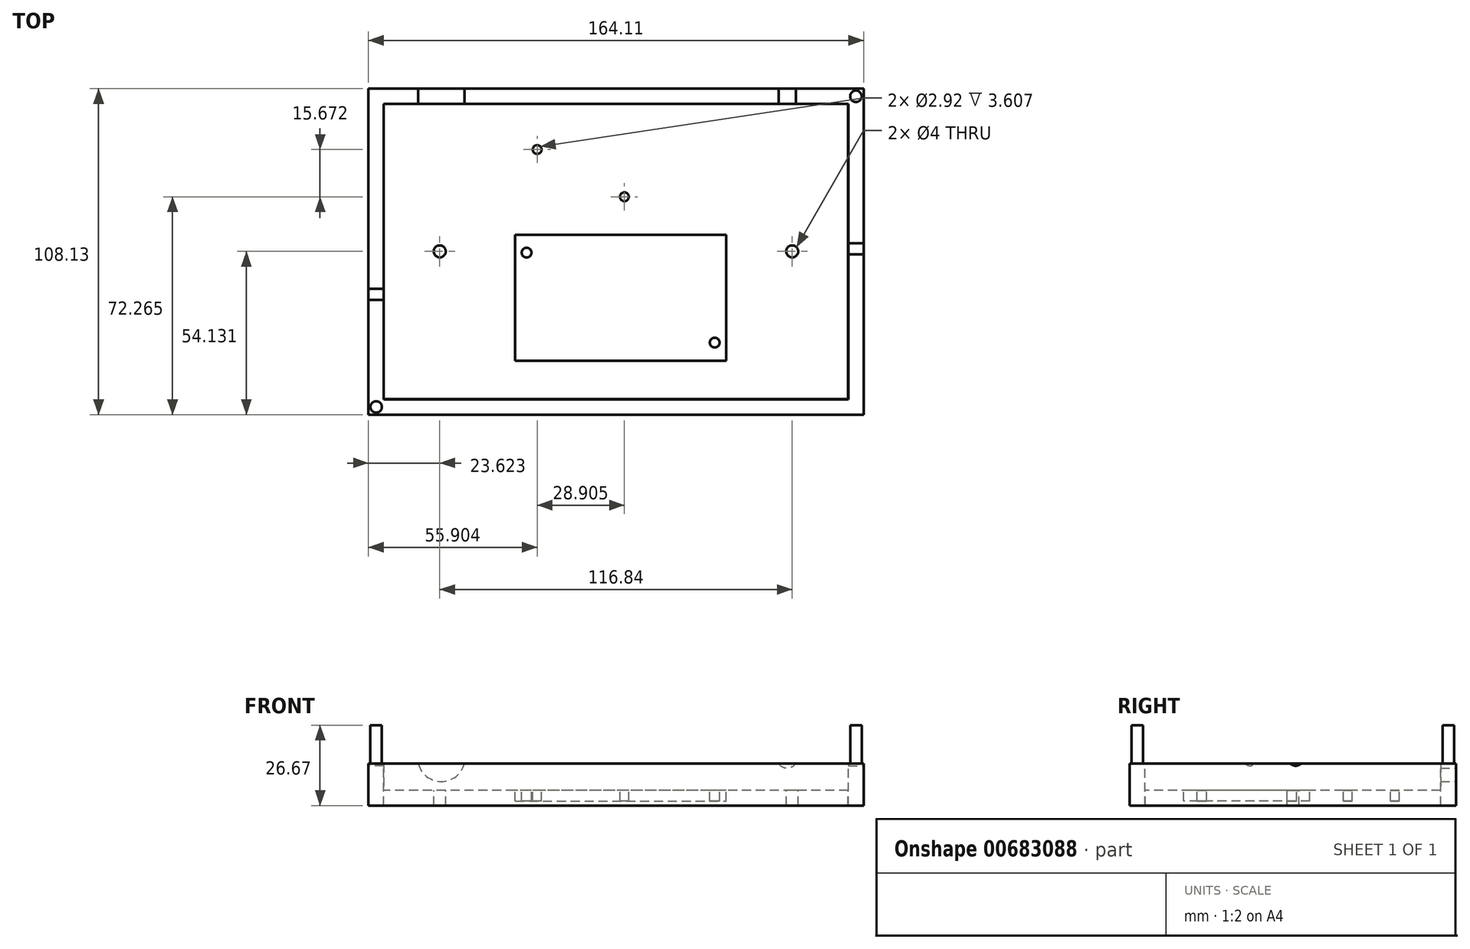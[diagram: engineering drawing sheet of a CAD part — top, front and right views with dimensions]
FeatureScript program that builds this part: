
annotation { "Feature Type Name" : "Feature", "Feature Type Description" : "" }
export const myFeature = defineFeature(function(context is Context, id is Id, definition is map)
    precondition{}
    {
        {
            var Q0;
            Q0=qCreatedBy(makeId("Top.planeOp"),FACE);
            var sketch = newSketch(context, id + "F0", { "sketchPlane" : qUnion([Q0])});
            skLineSegment(sketch, "E0", {"start": v(0, 0) * mm, "end": v(69.88, 0) * mm});
            skLineSegment(sketch, "E1", {"start": v(69.88, 0) * mm, "end": v(69.88, 41.78) * mm});
            skLineSegment(sketch, "E2", {"start": v(69.88, 41.78) * mm, "end": v(0, 41.78) * mm});
            skLineSegment(sketch, "E3", {"start": v(0, 41.78) * mm, "end": v(0, 0) * mm});
            skPoint(sketch, "E4", {"position": v(34.94, 20.9) * mm});
            skCircle(sketch, "E5", {"center": v(66.12, 35.81) * mm, "radius": 1.61 * mm});
            skCircle(sketch, "E6.MirrorC", {"center": v(3.76, 35.81) * mm, "radius": 1.61 * mm});
            skCircle(sketch, "E7.MirrorC", {"center": v(66.12, 5.97) * mm, "radius": 1.61 * mm});
            skCircle(sketch, "E8.MirrorC", {"center": v(3.76, 5.97) * mm, "radius": 1.61 * mm});
            skSolve(sketch);
        }
        {
            var Q0;
            Q0=qCreatedBy(makeId("Top.planeOp"),FACE);
            var sketch = newSketch(context, id + "F1", { "sketchPlane" : qUnion([Q0])});
            skLineSegment(sketch, "E9", {"start": v(0, 51.81) * mm, "end": v(43.43, 51.81) * mm});
            skLineSegment(sketch, "E10", {"start": v(0, 51.81) * mm, "end": v(0, 72.57) * mm});
            skLineSegment(sketch, "E11", {"start": v(0, 72.57) * mm, "end": v(43.43, 72.57) * mm});
            skLineSegment(sketch, "E12", {"start": v(43.43, 72.57) * mm, "end": v(43.43, 51.81) * mm});
            skCircle(sketch, "E13", {"center": v(36.17, 54.35) * mm, "radius": 1.46 * mm});
            skLineSegment(sketch, "E14", {"start": v(21.72, 72.57) * mm, "end": v(21.72, 51.81) * mm});
            skCircle(sketch, "E15", {"center": v(7.26, 70.03) * mm, "radius": 1.46 * mm});
            skSolve(sketch);
        }
        {
            var Q0;
            Q0=qCreatedBy(makeId("Top.planeOp"),FACE);
            var sketch = newSketch(context, id + "F2", { "sketchPlane" : qUnion([Q0])});
            skLineSegment(sketch, "E16", {"start": v(0, -12.7) * mm, "end": v(-43.59, -12.7) * mm});
            skLineSegment(sketch, "E17", {"start": v(-43.59, -12.7) * mm, "end": v(-43.59, 0) * mm});
            skLineSegment(sketch, "E18", {"start": v(-43.59, 72.57) * mm, "end": v(-43.59, 0) * mm});
            skLineSegment(sketch, "E19", {"start": v(0, 85.27) * mm, "end": v(-43.59, 85.27) * mm});
            skLineSegment(sketch, "E20", {"start": v(-43.59, 85.27) * mm, "end": v(-43.59, 72.57) * mm});
            skLineSegment(sketch, "E21", {"start": v(0, -12.7) * mm, "end": v(110.37, -12.7) * mm});
            skLineSegment(sketch, "E22", {"start": v(110.37, -12.7) * mm, "end": v(110.37, 85.27) * mm});
            skLineSegment(sketch, "E23", {"start": v(110.37, 85.27) * mm, "end": v(0, 85.27) * mm});
            skSolve(sketch);
        }
        {
            var Q0;
            Q0=makeQuery(id+"F2.imprint","IMPRINT",FACE,{"disambiguationData":[TD([[makeQuery(id+"F2.imprint","IMPRINT",EDGE,{"derivedFrom":sQuery(id+"F2.wireOp",EDGE,"E16")}),-1.0]])]});
            extrude(context, id + "F3", {"entities" : qUnion([Q0]), "oppositeDirection" : true, "depth" : 5.08 * mm, "offsetDistance" : 25.4 * mm});
        }
        {
            var Q0;
            Q0=qCreatedBy(makeId("Top.planeOp"),FACE);
            var sketch = newSketch(context, id + "F4", { "sketchPlane" : qUnion([Q0])});
            skLineSegment(sketch, "E24", {"start": v(-5.8, -12.83) * mm, "end": v(-43.56, -12.83) * mm});
            skLineSegment(sketch, "E25", {"start": v(-5.8, 85.14) * mm, "end": v(-43.56, 85.14) * mm});
            skLineSegment(sketch, "E26", {"start": v(-5.8, -12.83) * mm, "end": v(110.4, -12.83) * mm});
            skLineSegment(sketch, "E27", {"start": v(110.4, -12.83) * mm, "end": v(110.4, 85.14) * mm});
            skLineSegment(sketch, "E28", {"start": v(110.4, 85.14) * mm, "end": v(-5.8, 85.14) * mm});
            skLineSegment(sketch, "E29", {"start": v(-43.56, 85.14) * mm, "end": v(-43.56, -12.83) * mm});
            skLineSegment(sketch, "E30.0", {"start": v(-5.8, 90.22) * mm, "end": v(-43.56, 90.22) * mm});
            skLineSegment(sketch, "E31.0", {"start": v(110.4, 90.22) * mm, "end": v(-5.8, 90.22) * mm});
            skLineSegment(sketch, "E32.0", {"start": v(115.47, -12.83) * mm, "end": v(115.47, 85.14) * mm});
            skLineSegment(sketch, "E33.0", {"start": v(-5.8, -17.9) * mm, "end": v(110.4, -17.9) * mm});
            skLineSegment(sketch, "E34.0", {"start": v(-5.8, -17.9) * mm, "end": v(-43.56, -17.9) * mm});
            skLineSegment(sketch, "E35.0", {"start": v(-48.64, 85.14) * mm, "end": v(-48.64, -12.83) * mm});
            skLineSegment(sketch, "E36", {"start": v(-48.64, 85.14) * mm, "end": v(-48.64, 90.22) * mm});
            skLineSegment(sketch, "E37", {"start": v(-48.64, 90.22) * mm, "end": v(-43.56, 90.22) * mm});
            skLineSegment(sketch, "E38", {"start": v(110.4, 90.22) * mm, "end": v(115.47, 90.22) * mm});
            skLineSegment(sketch, "E39", {"start": v(115.47, 90.22) * mm, "end": v(115.47, 85.14) * mm});
            skLineSegment(sketch, "E40", {"start": v(-48.64, -12.83) * mm, "end": v(-48.64, -17.9) * mm});
            skLineSegment(sketch, "E41", {"start": v(-48.64, -17.9) * mm, "end": v(-43.56, -17.9) * mm});
            skLineSegment(sketch, "E42", {"start": v(110.4, -17.9) * mm, "end": v(115.47, -17.9) * mm});
            skLineSegment(sketch, "E43", {"start": v(115.47, -17.9) * mm, "end": v(115.47, -12.83) * mm});
            skSolve(sketch);
        }
        {
            var Q0;
            Q0=makeQuery(id+"F4.imprint","IMPRINT",FACE,{"disambiguationData":[TD([[makeQuery(id+"F4.imprint","IMPRINT",EDGE,{"derivedFrom":sQuery(id+"F4.wireOp",EDGE,"E24")}),-1.0]])]});
            var sketch = newSketch(context, id + "F5", { "sketchPlane" : qUnion([Q0])});
            skLineSegment(sketch, "E44", {"start": v(-5.8, -12.83) * mm, "end": v(-43.56, -12.83) * mm});
            skLineSegment(sketch, "E45", {"start": v(-5.8, 85.14) * mm, "end": v(-43.56, 85.14) * mm});
            skLineSegment(sketch, "E46", {"start": v(-5.8, -12.83) * mm, "end": v(110.4, -12.83) * mm});
            skLineSegment(sketch, "E47", {"start": v(110.4, -12.83) * mm, "end": v(110.4, 85.14) * mm});
            skLineSegment(sketch, "E48", {"start": v(110.4, 85.14) * mm, "end": v(-5.8, 85.14) * mm});
            skLineSegment(sketch, "E49", {"start": v(-43.56, 85.14) * mm, "end": v(-43.56, -12.83) * mm});
            skLineSegment(sketch, "E50.0", {"start": v(-5.8, 90.22) * mm, "end": v(-43.56, 90.22) * mm});
            skLineSegment(sketch, "E51.0", {"start": v(110.4, 90.22) * mm, "end": v(-5.8, 90.22) * mm});
            skLineSegment(sketch, "E52.0", {"start": v(-5.8, -17.9) * mm, "end": v(110.4, -17.9) * mm});
            skLineSegment(sketch, "E53.0", {"start": v(-5.8, -17.9) * mm, "end": v(-43.56, -17.9) * mm});
            skLineSegment(sketch, "E54.0", {"start": v(-48.64, 85.14) * mm, "end": v(-48.64, -12.83) * mm});
            skLineSegment(sketch, "E55", {"start": v(-48.64, 85.14) * mm, "end": v(-48.64, 90.22) * mm});
            skLineSegment(sketch, "E56", {"start": v(-48.64, 90.22) * mm, "end": v(-43.56, 90.22) * mm});
            skLineSegment(sketch, "E57", {"start": v(110.4, 90.22) * mm, "end": v(115.47, 90.22) * mm});
            skLineSegment(sketch, "E58", {"start": v(115.47, 90.22) * mm, "end": v(115.47, 48.98) * mm});
            skLineSegment(sketch, "E59", {"start": v(-48.64, -12.83) * mm, "end": v(-48.64, -17.9) * mm});
            skLineSegment(sketch, "E60", {"start": v(-48.64, -17.9) * mm, "end": v(-43.56, -17.9) * mm});
            skLineSegment(sketch, "E61", {"start": v(110.4, -17.9) * mm, "end": v(115.47, -17.9) * mm});
            skLineSegment(sketch, "E62", {"start": v(115.47, 48.98) * mm, "end": v(115.47, -17.9) * mm});
            skSolve(sketch);
        }
        {
            var Q0;
            Q0 = qSketchRegion(id + "F4", true);
            extrude(context, id + "F6", {"entities" : qUnion([Q0]), "operationType" : NewBodyOperationType.ADD, "oppositeDirection" : true, "depth" : 5.08 * mm, "offsetDistance" : 25.4 * mm});
        }
        {
            var Q0;
            Q0 = qSketchRegion(id + "F5", true);
            extrude(context, id + "F7", {"entities" : qUnion([Q0]), "operationType" : NewBodyOperationType.ADD, "depth" : 21.59 * mm, "offsetDistance" : 25.4 * mm});
        }
        {
            var Q0;
            Q0=makeQuery(id+"F7.boolean.opBoolean","MERGE",FACE,{"derivedFrom":[makeQuery(id+"F6.opExtrude","SWEPT_FACE",FACE,{"disambiguationData":[OSD([sQuery(id+"F4.wireOp",EDGE,"E30.0"),sQuery(id+"F4.wireOp",EDGE,"E31.0"),sQuery(id+"F4.wireOp",EDGE,"E37"),sQuery(id+"F4.wireOp",EDGE,"E38")])]}),makeQuery(id+"F7.opExtrude","SWEPT_FACE",FACE,{"disambiguationData":[OSD([sQuery(id+"F5.wireOp",EDGE,"E50.0"),sQuery(id+"F5.wireOp",EDGE,"E51.0"),sQuery(id+"F5.wireOp",EDGE,"E56"),sQuery(id+"F5.wireOp",EDGE,"E57")])]})]});
            var sketch = newSketch(context, id + "F8", { "sketchPlane" : qUnion([Q0])});
            skCircle(sketch, "E63", {"center": v(24.5, 10.8) * mm, "radius": 7.9 * mm});
            skSolve(sketch);
        }
        {
            var Q0;
            Q0=makeQuery(id+"F8.imprint","IMPRINT",FACE,{"disambiguationData":[TD([[makeQuery(id+"F8.imprint","IMPRINT",EDGE,{"derivedFrom":sQuery(id+"F8.wireOp",EDGE,"E63")}),1.0]])]});
            extrude(context, id + "F9", {"entities" : qUnion([Q0]), "operationType" : NewBodyOperationType.REMOVE, "oppositeDirection" : true, "depth" : 25.4 * mm, "offsetDistance" : 25.4 * mm});
        }
        {
            var Q0;
            Q0=makeQuery(id+"F7.boolean.opBoolean","MERGE",FACE,{"derivedFrom":[makeQuery(id+"F6.opExtrude","SWEPT_FACE",FACE,{"disambiguationData":[OSD([sQuery(id+"F4.wireOp",EDGE,"E30.0"),sQuery(id+"F4.wireOp",EDGE,"E31.0"),sQuery(id+"F4.wireOp",EDGE,"E37"),sQuery(id+"F4.wireOp",EDGE,"E38")])]}),makeQuery(id+"F7.opExtrude","SWEPT_FACE",FACE,{"disambiguationData":[OSD([sQuery(id+"F5.wireOp",EDGE,"E50.0"),sQuery(id+"F5.wireOp",EDGE,"E51.0"),sQuery(id+"F5.wireOp",EDGE,"E56"),sQuery(id+"F5.wireOp",EDGE,"E57")])]})]});
            var sketch = newSketch(context, id + "F10", { "sketchPlane" : qUnion([Q0])});
            skCircle(sketch, "E64", {"center": v(-90.13, 10.8) * mm, "radius": 3.43 * mm});
            skSolve(sketch);
        }
        {
            var Q0;
            Q0=makeQuery(id+"F10.imprint","IMPRINT",FACE,{"disambiguationData":[TD([[makeQuery(id+"F10.imprint","IMPRINT",EDGE,{"derivedFrom":sQuery(id+"F10.wireOp",EDGE,"E64")}),1.0]])]});
            extrude(context, id + "F11", {"entities" : qUnion([Q0]), "operationType" : NewBodyOperationType.REMOVE, "oppositeDirection" : true, "depth" : 25.4 * mm, "offsetDistance" : 25.4 * mm});
        }
        {
            var Q0;
            Q0=makeQuery(id+"F7.boolean.opBoolean","MERGE",FACE,{"derivedFrom":[makeQuery(id+"F6.opExtrude","SWEPT_FACE",FACE,{"disambiguationData":[OSD([sQuery(id+"F4.wireOp",EDGE,"E35.0"),sQuery(id+"F4.wireOp",EDGE,"E36"),sQuery(id+"F4.wireOp",EDGE,"E40")])]}),makeQuery(id+"F7.opExtrude","SWEPT_FACE",FACE,{"disambiguationData":[OSD([sQuery(id+"F5.wireOp",EDGE,"E54.0"),sQuery(id+"F5.wireOp",EDGE,"E55"),sQuery(id+"F5.wireOp",EDGE,"E59")])]})]});
            var sketch = newSketch(context, id + "F12", { "sketchPlane" : qUnion([Q0])});
            skCircle(sketch, "E65", {"center": v(-21.97, 10.8) * mm, "radius": 2.67 * mm});
            skSolve(sketch);
        }
        {
            var Q0;
            Q0=makeQuery(id+"F12.imprint","IMPRINT",FACE,{"disambiguationData":[TD([[makeQuery(id+"F12.imprint","IMPRINT",EDGE,{"derivedFrom":sQuery(id+"F12.wireOp",EDGE,"E65")}),1.0]])]});
            extrude(context, id + "F13", {"entities" : qUnion([Q0]), "operationType" : NewBodyOperationType.REMOVE, "oppositeDirection" : true, "depth" : 25.4 * mm, "offsetDistance" : 25.4 * mm});
        }
        {
            var Q0;
            Q0=makeQuery(id+"F7.boolean.opBoolean","MERGE",FACE,{"derivedFrom":[makeQuery(id+"F6.opExtrude","SWEPT_FACE",FACE,{"disambiguationData":[OSD([sQuery(id+"F4.wireOp",EDGE,"E32.0"),sQuery(id+"F4.wireOp",EDGE,"E39"),sQuery(id+"F4.wireOp",EDGE,"E43")])]}),makeQuery(id+"F7.opExtrude","SWEPT_FACE",FACE,{"disambiguationData":[OSD([sQuery(id+"F5.wireOp",EDGE,"E58"),sQuery(id+"F5.wireOp",EDGE,"E62")])]})]});
            var sketch = newSketch(context, id + "F14", { "sketchPlane" : qUnion([Q0])});
            skCircle(sketch, "E66", {"center": v(37.1, 10.8) * mm, "radius": 2.67 * mm});
            skSolve(sketch);
        }
        {
            var Q0;
            Q0=makeQuery(id+"F14.imprint","IMPRINT",FACE,{"disambiguationData":[TD([[makeQuery(id+"F14.imprint","IMPRINT",EDGE,{"derivedFrom":sQuery(id+"F14.wireOp",EDGE,"E66")}),1.0]])]});
            extrude(context, id + "F15", {"entities" : qUnion([Q0]), "operationType" : NewBodyOperationType.REMOVE, "oppositeDirection" : true, "depth" : 25.4 * mm, "offsetDistance" : 25.4 * mm});
        }
        {
            var Q0;
            Q0=makeQuery(id+"F1.imprint","IMPRINT",FACE,{"disambiguationData":[TD([[makeQuery(id+"F1.imprint","IMPRINT",EDGE,{"derivedFrom":sQuery(id+"F1.wireOp",EDGE,"E15")}),1.0]])]});
            var Q1;
            Q1=makeQuery(id+"F1.imprint","IMPRINT",FACE,{"disambiguationData":[TD([[makeQuery(id+"F1.imprint","IMPRINT",EDGE,{"derivedFrom":sQuery(id+"F1.wireOp",EDGE,"E13")}),1.0]])]});
            extrude(context, id + "F16", {"entities" : qUnion([Q0, Q1]), "operationType" : NewBodyOperationType.REMOVE, "oppositeDirection" : true, "depth" : 3.6 * mm, "offsetDistance" : 25.4 * mm});
        }
        {
            var Q0;
            Q0=makeQuery(id+"F0.imprint","IMPRINT",FACE,{"disambiguationData":[TD([[makeQuery(id+"F0.imprint","IMPRINT",EDGE,{"derivedFrom":sQuery(id+"F0.wireOp",EDGE,"E6.MirrorC")}),-1.0]])]});
            var Q1;
            Q1=makeQuery(id+"F0.imprint","IMPRINT",FACE,{"disambiguationData":[TD([[makeQuery(id+"F0.imprint","IMPRINT",EDGE,{"derivedFrom":sQuery(id+"F0.wireOp",EDGE,"E8.MirrorC")}),1.0]])]});
            var Q2;
            Q2=makeQuery(id+"F0.imprint","IMPRINT",FACE,{"disambiguationData":[TD([[makeQuery(id+"F0.imprint","IMPRINT",EDGE,{"derivedFrom":sQuery(id+"F0.wireOp",EDGE,"E7.MirrorC")}),-1.0]])]});
            var Q3;
            Q3=makeQuery(id+"F0.imprint","IMPRINT",FACE,{"disambiguationData":[TD([[makeQuery(id+"F0.imprint","IMPRINT",EDGE,{"derivedFrom":sQuery(id+"F0.wireOp",EDGE,"E5")}),1.0]])]});
            extrude(context, id + "F17", {"entities" : qUnion([Q0, Q1, Q2, Q3]), "operationType" : NewBodyOperationType.REMOVE, "oppositeDirection" : true, "depth" : 3.6 * mm, "offsetDistance" : 25.4 * mm});
        }
        {
            var Q0;
            Q0=makeQuery(id+"F7.opExtrude","CAP_FACE",FACE,{"disambiguationData":[OSD([sQuery(id+"F5.wireOp",EDGE,"E44"),sQuery(id+"F5.wireOp",EDGE,"E45"),sQuery(id+"F5.wireOp",EDGE,"E46"),sQuery(id+"F5.wireOp",EDGE,"E47"),sQuery(id+"F5.wireOp",EDGE,"E48"),sQuery(id+"F5.wireOp",EDGE,"E49"),sQuery(id+"F5.wireOp",EDGE,"E50.0"),sQuery(id+"F5.wireOp",EDGE,"E51.0"),sQuery(id+"F5.wireOp",EDGE,"E52.0"),sQuery(id+"F5.wireOp",EDGE,"E53.0"),sQuery(id+"F5.wireOp",EDGE,"E54.0"),sQuery(id+"F5.wireOp",EDGE,"E55"),sQuery(id+"F5.wireOp",EDGE,"E56"),sQuery(id+"F5.wireOp",EDGE,"E57"),sQuery(id+"F5.wireOp",EDGE,"E58"),sQuery(id+"F5.wireOp",EDGE,"E59"),sQuery(id+"F5.wireOp",EDGE,"E60"),sQuery(id+"F5.wireOp",EDGE,"E61"),sQuery(id+"F5.wireOp",EDGE,"E62")])],"isStart":false});
            var sketch = newSketch(context, id + "F18", { "sketchPlane" : qUnion([Q0])});
            skCircle(sketch, "E67", {"center": v(-46.1, 87.68) * mm, "radius": 1.9 * mm});
            skCircle(sketch, "E68.MirrorC", {"center": v(112.93, 87.68) * mm, "radius": 1.9 * mm});
            skCircle(sketch, "E69.MirrorC", {"center": v(-46.1, -15.37) * mm, "radius": 1.9 * mm});
            skCircle(sketch, "E70.MirrorC", {"center": v(112.93, -15.37) * mm, "radius": 1.9 * mm});
            skSolve(sketch);
        }
        {
            var Q0;
            Q0=makeQuery(id+"F18.imprint","IMPRINT",FACE,{"disambiguationData":[TD([[makeQuery(id+"F18.imprint","IMPRINT",EDGE,{"derivedFrom":sQuery(id+"F18.wireOp",EDGE,"E69.MirrorC")}),-1.0]])]});
            var Q1;
            Q1=makeQuery(id+"F18.imprint","IMPRINT",FACE,{"disambiguationData":[TD([[makeQuery(id+"F18.imprint","IMPRINT",EDGE,{"derivedFrom":sQuery(id+"F18.wireOp",EDGE,"E67")}),1.0]])]});
            var Q2;
            Q2=makeQuery(id+"F18.imprint","IMPRINT",FACE,{"disambiguationData":[TD([[makeQuery(id+"F18.imprint","IMPRINT",EDGE,{"derivedFrom":sQuery(id+"F18.wireOp",EDGE,"E68.MirrorC")}),-1.0]])]});
            var Q3;
            Q3=makeQuery(id+"F18.imprint","IMPRINT",FACE,{"disambiguationData":[TD([[makeQuery(id+"F18.imprint","IMPRINT",EDGE,{"derivedFrom":sQuery(id+"F18.wireOp",EDGE,"E70.MirrorC")}),1.0]])]});
            extrude(context, id + "F19", {"entities" : qUnion([Q0, Q1, Q2, Q3]), "operationType" : NewBodyOperationType.REMOVE, "oppositeDirection" : true, "depth" : 12.7 * mm, "offsetDistance" : 25.4 * mm});
        }
        {
            var Q0;
            Q0=makeQuery(id+"F6.boolean.opBoolean","MERGE",FACE,{"derivedFrom":[makeQuery(id+"F3.opExtrude","CAP_FACE",FACE,{"disambiguationData":[OSD([sQuery(id+"F2.wireOp",EDGE,"E16"),sQuery(id+"F2.wireOp",EDGE,"E17"),sQuery(id+"F2.wireOp",EDGE,"E18"),sQuery(id+"F2.wireOp",EDGE,"E19"),sQuery(id+"F2.wireOp",EDGE,"E20"),sQuery(id+"F2.wireOp",EDGE,"E21"),sQuery(id+"F2.wireOp",EDGE,"E22"),sQuery(id+"F2.wireOp",EDGE,"E23")])],"isStart":true}),makeQuery(id+"F6.opExtrude","CAP_FACE",FACE,{"disambiguationData":[OSD([sQuery(id+"F4.wireOp",EDGE,"E24"),sQuery(id+"F4.wireOp",EDGE,"E25"),sQuery(id+"F4.wireOp",EDGE,"E26"),sQuery(id+"F4.wireOp",EDGE,"E27"),sQuery(id+"F4.wireOp",EDGE,"E28"),sQuery(id+"F4.wireOp",EDGE,"E29"),sQuery(id+"F4.wireOp",EDGE,"E30.0"),sQuery(id+"F4.wireOp",EDGE,"E31.0"),sQuery(id+"F4.wireOp",EDGE,"E32.0"),sQuery(id+"F4.wireOp",EDGE,"E33.0"),sQuery(id+"F4.wireOp",EDGE,"E34.0"),sQuery(id+"F4.wireOp",EDGE,"E35.0"),sQuery(id+"F4.wireOp",EDGE,"E36"),sQuery(id+"F4.wireOp",EDGE,"E37"),sQuery(id+"F4.wireOp",EDGE,"E38"),sQuery(id+"F4.wireOp",EDGE,"E39"),sQuery(id+"F4.wireOp",EDGE,"E40"),sQuery(id+"F4.wireOp",EDGE,"E41"),sQuery(id+"F4.wireOp",EDGE,"E42"),sQuery(id+"F4.wireOp",EDGE,"E43")])],"isStart":true})]});
            var sketch = newSketch(context, id + "F20", { "sketchPlane" : qUnion([Q0])});
            skCircle(sketch, "E71", {"center": v(91.82, 36.22) * mm, "radius": 2 * mm});
            skCircle(sketch, "E72", {"center": v(-25.02, 36.22) * mm, "radius": 2 * mm});
            skSolve(sketch);
        }
        {
            var Q0;
            Q0=makeQuery(id+"F20.imprint","IMPRINT",FACE,{"disambiguationData":[TD([[makeQuery(id+"F20.imprint","IMPRINT",EDGE,{"derivedFrom":sQuery(id+"F20.wireOp",EDGE,"E72")}),1.0]])]});
            var Q1;
            Q1=makeQuery(id+"F20.imprint","IMPRINT",FACE,{"disambiguationData":[TD([[makeQuery(id+"F20.imprint","IMPRINT",EDGE,{"derivedFrom":sQuery(id+"F20.wireOp",EDGE,"E71")}),1.0]])]});
            extrude(context, id + "F21", {"entities" : qUnion([Q0, Q1]), "operationType" : NewBodyOperationType.REMOVE, "oppositeDirection" : true, "depth" : 25.4 * mm, "offsetDistance" : 25.4 * mm});
        }
    });
